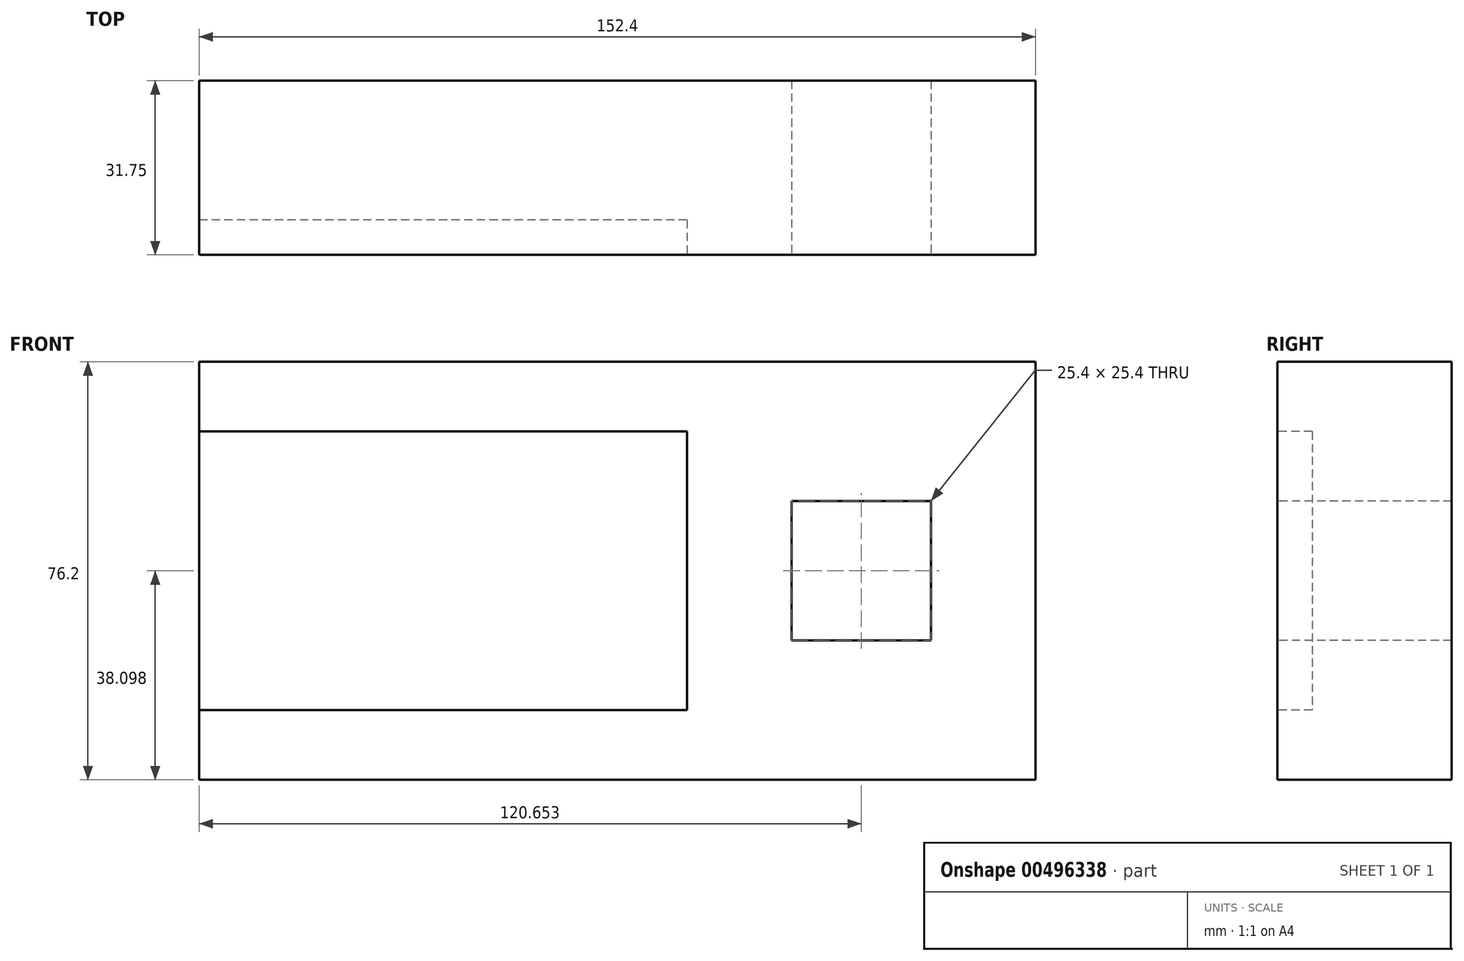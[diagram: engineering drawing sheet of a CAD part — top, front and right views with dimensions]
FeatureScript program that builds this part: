
annotation { "Feature Type Name" : "Feature", "Feature Type Description" : "" }
export const myFeature = defineFeature(function(context is Context, id is Id, definition is map)
    precondition{}
    {
        {
            var Q0;
            Q0=qCreatedBy(makeId("Front.planeOp"),FACE);
            var sketch = newSketch(context, id + "F0", { "sketchPlane" : qUnion([Q0])});
            skLineSegment(sketch, "E0.bottom", {"start": v(108.78, -53.48) * mm, "end": v(108.78, -129.68) * mm});
            skLineSegment(sketch, "E0.top", {"start": v(-43.62, -53.48) * mm, "end": v(-43.62, -129.68) * mm});
            skLineSegment(sketch, "E0.left", {"start": v(108.78, -53.48) * mm, "end": v(-43.62, -53.48) * mm});
            skLineSegment(sketch, "E0.right", {"start": v(108.78, -129.68) * mm, "end": v(-43.62, -129.68) * mm});
            skSolve(sketch);
        }
        {
            var Q0;
            Q0 = qSketchRegion(id + "F0", true);
            extrude(context, id + "F1", {"entities" : qUnion([Q0]), "depth" : 31.75 * mm});
        }
        {
            var Q0;
            Q0=makeQuery(id+"F1.opExtrude","CAP_FACE",FACE,{"disambiguationData":[OSD([sQuery(id+"F0.wireOp",EDGE,"E0.bottom"),sQuery(id+"F0.wireOp",EDGE,"E0.top"),sQuery(id+"F0.wireOp",EDGE,"E0.left"),sQuery(id+"F0.wireOp",EDGE,"E0.right")])],"isStart":false});
            var sketch = newSketch(context, id + "F2", { "sketchPlane" : qUnion([Q0])});
            skLineSegment(sketch, "E1.bottom", {"start": v(45.28, -66.18) * mm, "end": v(45.28, -116.98) * mm});
            skLineSegment(sketch, "E1.top", {"start": v(-43.62, -66.18) * mm, "end": v(-43.62, -116.98) * mm});
            skLineSegment(sketch, "E1.left", {"start": v(45.28, -66.18) * mm, "end": v(-43.62, -66.18) * mm});
            skLineSegment(sketch, "E1.right", {"start": v(45.28, -116.98) * mm, "end": v(-43.62, -116.98) * mm});
            skSolve(sketch);
        }
        {
            var Q0;
            Q0=makeQuery(id+"F2.imprint","IMPRINT",FACE,{"disambiguationData":[TD([[makeQuery(id+"F2.imprint","IMPRINT",EDGE,{"derivedFrom":sQuery(id+"F2.wireOp",EDGE,"E1.bottom")}),-1.0]])]});
            extrude(context, id + "F3", {"entities" : qUnion([Q0]), "operationType" : NewBodyOperationType.REMOVE, "oppositeDirection" : true, "depth" : 6.35 * mm});
        }
        {
            var Q0;
            Q0=makeQuery(id+"F1.opExtrude","CAP_FACE",FACE,{"disambiguationData":[OSD([sQuery(id+"F0.wireOp",EDGE,"E0.bottom"),sQuery(id+"F0.wireOp",EDGE,"E0.top"),sQuery(id+"F0.wireOp",EDGE,"E0.left"),sQuery(id+"F0.wireOp",EDGE,"E0.right")])],"isStart":false});
            var sketch = newSketch(context, id + "F4", { "sketchPlane" : qUnion([Q0])});
            skLineSegment(sketch, "E2.bottom", {"start": v(64.33, -78.88) * mm, "end": v(89.73, -78.88) * mm});
            skLineSegment(sketch, "E2.top", {"start": v(64.33, -104.28) * mm, "end": v(89.73, -104.28) * mm});
            skLineSegment(sketch, "E2.left", {"start": v(64.33, -78.88) * mm, "end": v(64.33, -104.28) * mm});
            skLineSegment(sketch, "E2.right", {"start": v(89.73, -78.88) * mm, "end": v(89.73, -104.28) * mm});
            skSolve(sketch);
        }
        {
            var Q0;
            Q0=makeQuery(id+"F4.imprint","IMPRINT",FACE,{"disambiguationData":[TD([[makeQuery(id+"F4.imprint","IMPRINT",EDGE,{"derivedFrom":sQuery(id+"F4.wireOp",EDGE,"E2.bottom")}),-1.0]])]});
            extrude(context, id + "F5", {"entities" : qUnion([Q0]), "operationType" : NewBodyOperationType.REMOVE, "oppositeDirection" : true, "depth" : 31.75 * mm});
        }
    });
